# Revit family: RA-DV_Axial_DN10-15_Aero_RFA_1
name_source: partatom
category: Pipe Accessories
units: mm (PartAtom-declared; Revit-internal decimal feet)

## family parameters
Always vertical = Yes
Cut with Voids When Loaded = No
OmniClass Number = 23.65.55.14.17
OmniClass Title = Adjusting/Controlling Valves for Liquid Services
Part Type = Valve - Breaks Into
Round Connector Dimension = Use Diameter
Shared = No
Work Plane-Based = No

## types (2) — shared parameters
015G4540 = Aero Sensors_RA_RFA : Aero Sensors_Tamperproof_Built-in_7-28 °C_015G4540
015G4542 = Aero Sensors_RA_RFA : Aero Sensors_Tamperproof_Remote_7-26 °C_015G4542
015G4544 = Aero Sensors_RA_RFA : Aero Sensors_Tamperproof_Built-in_7-21 °C_015G4544
Application = 2-Pipe System
Description = Thermostatic Radiator Valve
IfcExportAs = IfcValveType
IfcExportType = RA-DV
LL01 = 10 mm  [stored 0.0328084 ft]
LL02 = 5 mm  [stored 0.0164042 ft]
LL2 = 4 mm  [stored 0.0131234 ft]
LOD 200 = No
LOD 350 = Yes
LR1 = 23 mm
LR5 = 10 mm  [stored 0.0328084 ft]
LR6 = 4 mm  [stored 0.0131234 ft]
LR7 = 3 mm  [stored 0.00984252 ft]
LR8 = 4 mm  [stored 0.0131234 ft]
Manufacturer = Danfoss
Max Differential Pressure = 0.6 bar
Max Flow (Text) = 135 l/h
Max Medium Temperature = 95 °C
Max Operating Pressure = 10 bar
Min Differential Pressure = 0.1 bar
Min Medium Temperature = 2 °C
RL1 = 10 mm  [stored 0.0328084 ft]
RR1 = 12 mm  [stored 0.0393701 ft]
RR2 = 15 mm  [stored 0.0492126 ft]
RR3 = 11 mm
RR4 = 8 mm  [stored 0.0262467 ft]
RR5 = 10 mm  [stored 0.0328084 ft]
RR6 = 8 mm  [stored 0.0262467 ft]
RR7 = 8 mm  [stored 0.0262467 ft]
RR8 = 5 mm  [stored 0.0164042 ft]
RR9 = 1 mm  [stored 0.00328084 ft]
RT1 = 12 mm  [stored 0.0393701 ft]
Sensor Type = Aero Sensors_RA_RFA : Aero Sensors_Built-in_7-28 °C
Setting Range = 1-7,N
URL = https://store.danfoss.com
Valve Body Material = Danfoss Nickel Plated Brass
W = 56 mm  [stored 0.183727 ft]
Weight = 0.19 kg
zero-valued in all types: SH1, SH2

## per-type parameters (varying)
- RA-DV_Axial_DN10_013G7709: AL=27 mm  [stored 0.0885827 ft]; AR=21 mm  [stored 0.0688976 ft]; BL1=14 mm  [stored 0.0459318 ft]; BL2=8 mm  [stored 0.0262467 ft]; D=10 mm  [stored 0.0328084 ft]; H=54 mm  [stored 0.177165 ft]; H'=51 mm; HR1=16 mm; HR2=13 mm  [stored 0.0426509 ft]; HT=29 mm; Ha=26 mm  [stored 0.0853018 ft]; Hex1=27 mm  [stored 0.0885827 ft]; Hex2=22 mm  [stored 0.0721785 ft]; LL1=21 mm  [stored 0.0688976 ft]; LL3=9 mm  [stored 0.0295276 ft]; LL4=19 mm; LR0=5 mm  [stored 0.0164042 ft]; LR2=6 mm  [stored 0.019685 ft]; LR3=8 mm  [stored 0.0262467 ft]; LR4=2 mm  [stored 0.00656168 ft]; Model=013G7709; Model Type=RA-DV_Axial_DN10; RB1=10 mm  [stored 0.0328084 ft]; RL2=13 mm  [stored 0.0426509 ft]; RL4=8 mm  [stored 0.0262467 ft]; RR0=4 mm  [stored 0.0131234 ft]; RT0=17 mm; Sa2=22 mm  [stored 0.0721785 ft]; Sa3=33 mm
- RA-DV_Axial_DN15_013G7710: AL=28 mm  [stored 0.0918635 ft]; AR=23 mm; BL1=18 mm  [stored 0.0590551 ft]; BL2=10 mm  [stored 0.0328084 ft]; D=15 mm  [stored 0.0492126 ft]; H=61 mm  [stored 0.200131 ft]; H'=58 mm  [stored 0.190289 ft]; HR1=17 mm; HR2=15 mm  [stored 0.0492126 ft]; HT=30 mm  [stored 0.0984252 ft]; Ha=33 mm; Hex1=30 mm  [stored 0.0984252 ft]; Hex2=27 mm  [stored 0.0885827 ft]; LL1=23 mm; LL3=10 mm  [stored 0.0328084 ft]; LL4=21 mm  [stored 0.0688976 ft]; LR0=4 mm  [stored 0.0131234 ft]; LR2=7 mm  [stored 0.0229659 ft]; LR3=7 mm  [stored 0.0229659 ft]; LR4=3 mm  [stored 0.00984252 ft]; Model=013G7710; Model Type=RA-DV_Axial_DN15; RB1=12 mm  [stored 0.0393701 ft]; RL2=15 mm  [stored 0.0492126 ft]; RL4=11 mm; RR0=6 mm  [stored 0.019685 ft]; RT0=18 mm  [stored 0.0590551 ft]; Sa2=27 mm  [stored 0.0885827 ft]; Sa3=36 mm  [stored 0.11811 ft]

note: [stored X ft] marks values corroborated as IEEE doubles in the binary element streams (Revit-internal decimal feet)

## geometry (parser evidence)
native form markers: Sweep x9
no freeform markers — native parametric forms only
